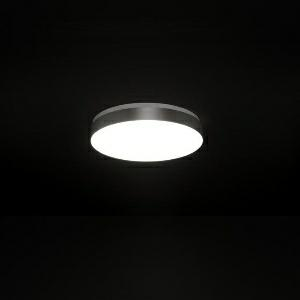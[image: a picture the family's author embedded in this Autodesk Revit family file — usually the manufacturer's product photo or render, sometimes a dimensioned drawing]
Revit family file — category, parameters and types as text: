
# Revit family: spectral_norea_norea-rp_306_1900_840_os_1323
name_source: partatom
category: Lighting Fixtures
revit_build: Autodesk Revit 2016 (Build: 20150220_1215(x64)
units: mm (PartAtom-declared; Revit-internal decimal feet)

## family parameters
Cut with Voids When Loaded = No
Host = Face
Light Source = No
Part Type = Normal
Room Calculation Point = No
Round Connector Dimension = Use Diameter
Shared = No

## types (1)
- SPECTRAL NOREA (1 x )
    Apparent Load = 0 VA
    Approval mark = CE
    CIE Flux Codes = 47 78 95 100 68
    Control Gear = Electronic transformer
    Default Elevation = 1800 mm
    Description = SPT0000129
NOREA Pendant luminaire

Round element with an opal acrylic panel in a natural anodised aluminium profile frame surround. The frame is fixed at the powder-coated metal body by a bayonet fixture with spring clip. The luminaire is suspended by a six trapezoidal wire pendants with ceiling fixture and transparent connecting cable round ceiling junction box. Cable length adjustable at the junction box, steel wire steplessly height adjustable. The metal body accommodates the electrical components and electronic ballast. The LED module is formed as a round LED flat board and can be removed for mounting or exchange using a keyhole screw connection. Plug-in electrical connection of the LED flat board. Luminaire with heat-resistant wiring. Homogenous illumination of the light surface. Suitable for ceiling or wall mounting. Also in a dimmable version. Protection rating IP20, safety class I.

Colour:
Housing – similar to RAL 9016 White silk matt;
Frame – natural anodised
    Height = 78 mm  [stored 0.255906 ft]
    Lamp = 1 x
    Lamp count = 1
    Length = 306 mm
    Luminous efficacy = 0 lm/W
    Manufacturer = Ridi
    ModVariant = No
    Model = NOREA-RP 306/1900/840 OS
    Mounting Place = Ceiling
    Mounting Type = Pendant
    Number of Poles = 1
    OnlyDefault = Yes
    Power Factor = 1
    Product Name = SPECTRAL NOREA
    Product group = Pendant luminaire
    ProductGroupID = 9
    Protection Class = Protection class
    Protection Degree = IP 20
    RlxData = <blob elided: 30197 chars, md5=cb54f026>
    Socket = socket
    Standby Power = 0 W
    System Light Flux = 0 lm
    System Power = 0 W
    Type Image = rundmittel01_-_kopie.jpg
    URL = http://reluxnet.relux.com
    VarID = 1
    Voltage = 0 V
    Weight = 0.00 kg
    Width = 0 mm  [stored 0 ft]

note: [stored X ft] marks values corroborated as IEEE doubles in the binary element streams (Revit-internal decimal feet)

## geometry (parser evidence)
native form markers: Sweep x13
no freeform markers — native parametric forms only
